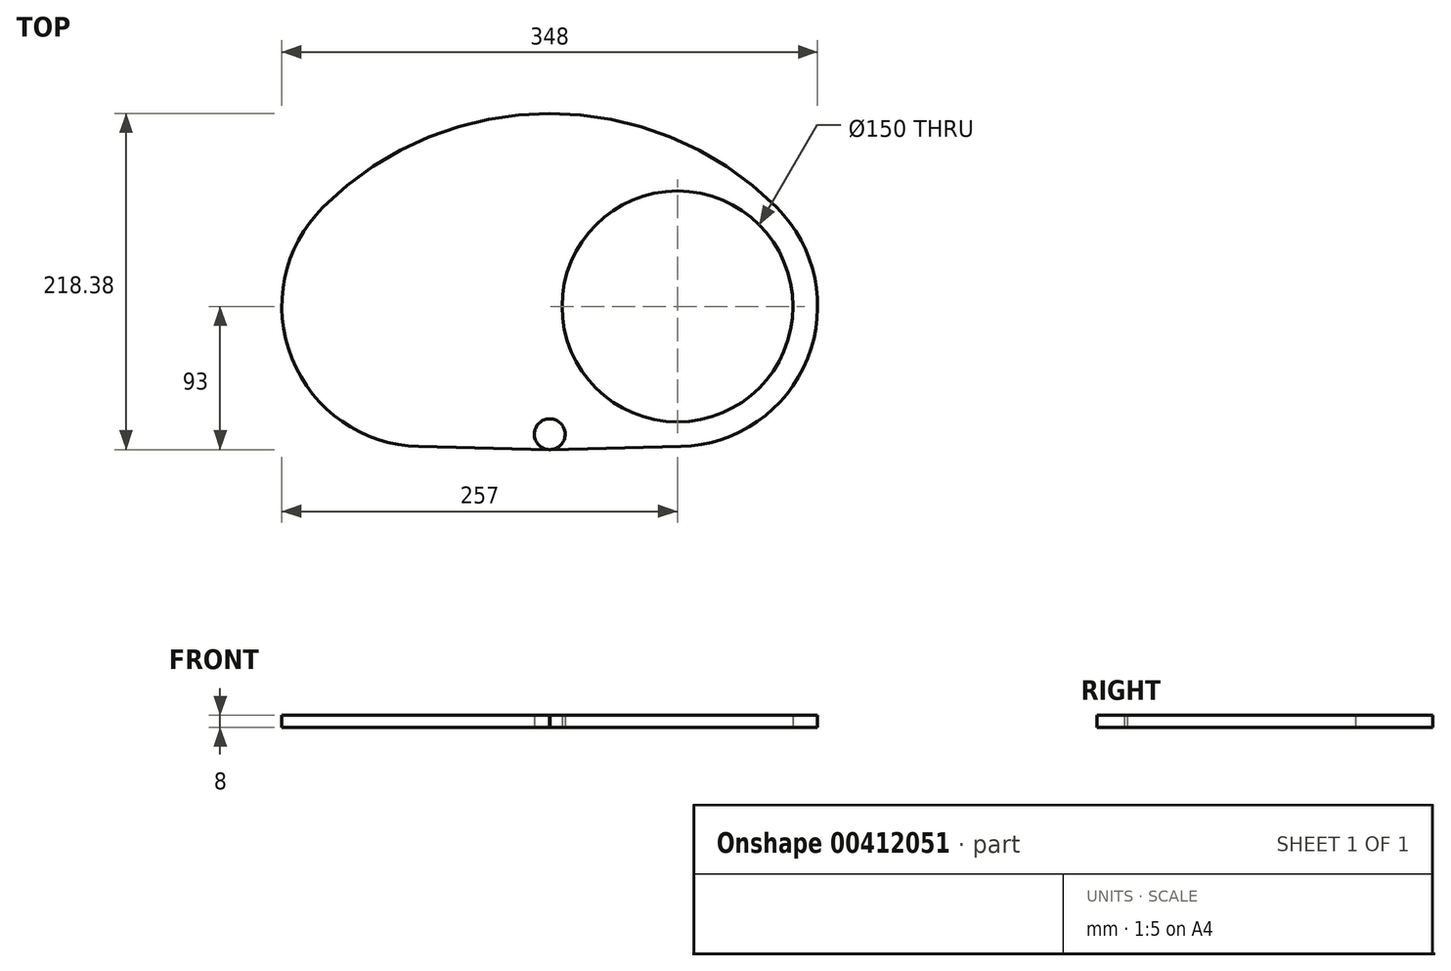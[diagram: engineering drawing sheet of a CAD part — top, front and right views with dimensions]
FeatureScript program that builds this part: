
annotation { "Feature Type Name" : "Feature", "Feature Type Description" : "" }
export const myFeature = defineFeature(function(context is Context, id is Id, definition is map)
    precondition{}
    {
        {
            var Q0;
            Q0=qCreatedBy(makeId("Top.planeOp"),FACE);
            var sketch = newSketch(context, id + "F0", { "sketchPlane" : qUnion([Q0])});
            skCircle(sketch, "E0", {"center": v(0, 0) * mm, "radius": 75 * mm});
            skCircle(sketch, "E1", {"center": v(-166, 0) * mm, "radius": 75 * mm});
            skArc(sketch, "E2", {"start": v(-91, 0) * mm, "mid": v(34.82, -84.07) * mm, "end": v(64.35, 64.35) * mm});
            skLineSegment(sketch, "E3", {"start": v(-166, 0) * mm, "end": v(0, 0) * mm, "construction": true});
            skLineSegment(sketch, "E4", {"start": v(-83, 0) * mm, "end": v(-83, -83) * mm, "construction": true});
            skArc(sketch, "E5", {"start": v(-230.35, 64.35) * mm, "mid": v(-200.82, -84.07) * mm, "end": v(-75, 0) * mm});
            skCircle(sketch, "E6", {"center": v(-83, -83) * mm, "radius": 10 * mm});
            skLineSegment(sketch, "E7", {"start": v(-168.17, -90.97) * mm, "end": v(-83.24, -93) * mm});
            skLineSegment(sketch, "E8", {"start": v(-82.76, -93) * mm, "end": v(2.17, -90.97) * mm});
            skArc(sketch, "E9", {"start": v(64.35, 64.35) * mm, "mid": v(-83, 125.38) * mm, "end": v(-230.35, 64.35) * mm});
            skSolve(sketch);
        }
        {
            var Q0;
            Q0=makeQuery(id+"F0.imprint","IMPRINT",FACE,{"disambiguationData":[TD([[makeQuery(id+"F0.imprint","IMPRINT",EDGE,{"derivedFrom":sQuery(id+"F0.wireOp",EDGE,"E0")}),-1.0]])]});
            var Q1;
            Q1=makeQuery(id+"F0.imprint","IMPRINT",FACE,{"disambiguationData":[TD([[makeQuery(id+"F0.imprint","IMPRINT",EDGE,{"derivedFrom":sQuery(id+"F0.wireOp",EDGE,"E1")}),1.0]])]});
            var Q2;
            {var subQ0=sQuery(id+"F0.wireOp",EDGE,"E7");Q2=makeQuery(id+"F0.imprint","IMPRINT",FACE,{"disambiguationData":[TD([[makeQuery(id+"F0.imprint","IMPRINT",EDGE,{"derivedFrom":subQ0}),1.0]])]});}
            extrude(context, id + "F1", {"entities" : qUnion([Q0, Q1, Q2]), "depth" : 8 * mm});
        }
    });
